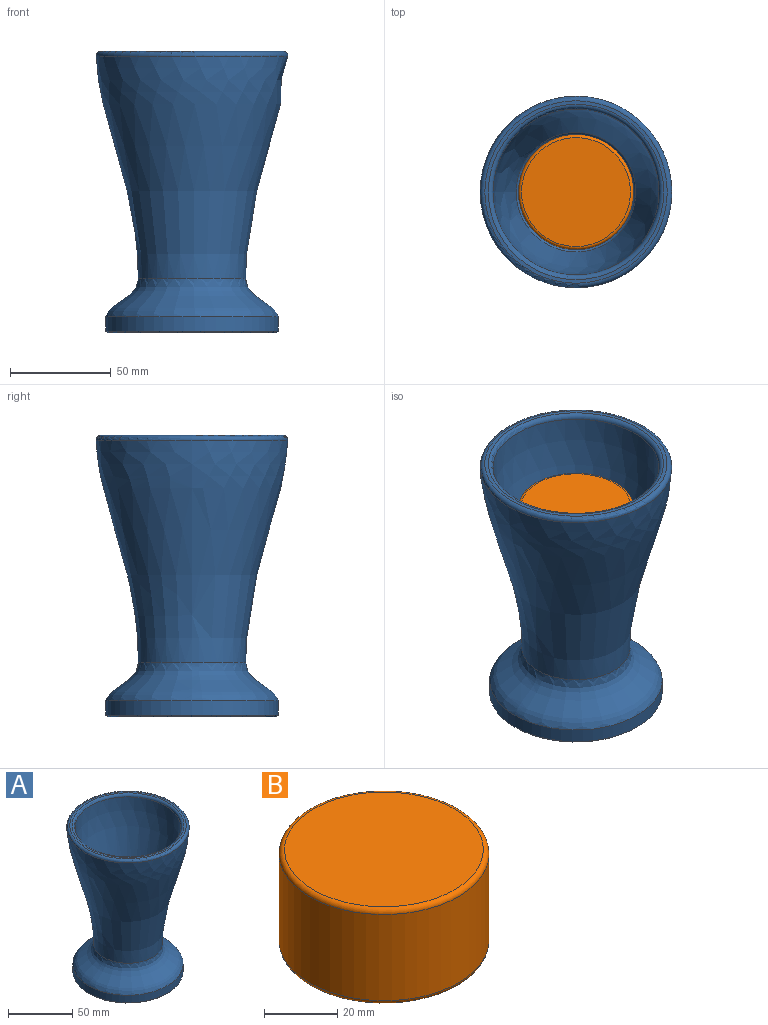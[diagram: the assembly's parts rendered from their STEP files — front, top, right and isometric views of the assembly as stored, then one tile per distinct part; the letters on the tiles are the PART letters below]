
ASSEMBLY  parts=2 mates=1
PART A: 11 faces, bbox 103x103x139.7 mm
  f0: revolved ~110.35x95.18mm, area 25601.3mm2, adj f1,f5
  f1: revolved ~85.73x85.73mm, area 5566.4mm2, adj f0,f2
  f2: cylinder r=42.86mm len=85.73mm, axis (0,0,-1), area 1915.4mm2, adj f1,f3
  f3: cone r=42.1mm half-angle=45deg, axis (0,0,1), area 287.6mm2, adj f2,f4
  f4: plane 84.2x84.2mm, normal (0,0,-1), area 5568.3mm2, adj f3
  f5: torus R=45.31mm, axis (0,0,-1), area 1075mm2, adj f0,f6
  f6: plane 90.61x90.61mm, normal (0,0,1), area 495.7mm2, adj f5,f7
  f7: torus R=43.53mm, axis (0,0,-1), area 932.9mm2, adj f6
  f8: plane 53.38x53.38mm, normal (0,0,-1), area 2237.7mm2, adj f9
  f9: torus R=26.69mm, axis (0,0,-1), area 735.3mm2, adj f8
  f10: revolved ~82.49x82.49mm, area 24809.9mm2
PART B: 5 faces, bbox 61.9x61.9x31.8 mm
  f0: plane 54.1x54.1mm, normal (0,0,-1), area 2298.9mm2, adj f3
  f1: cylinder r=28.57mm len=57.15mm, axis (0,0,-1), area 5153.2mm2, adj f3,f4
  f2: plane 54.1x54.1mm, normal (0,0,1), area 2298.9mm2, adj f4
  f3: torus R=27.05mm, axis (0,0,-1), area 421.5mm2, adj f0,f1
  f4: torus R=27.05mm, axis (0,0,-1), area 421.5mm2, adj f1,f2
PLACE A at identity fixed
PLACE B at identity
MATE fastened A.f2 <-> B.f1  axis (0,0,1) through (0,0,82.55)mm
